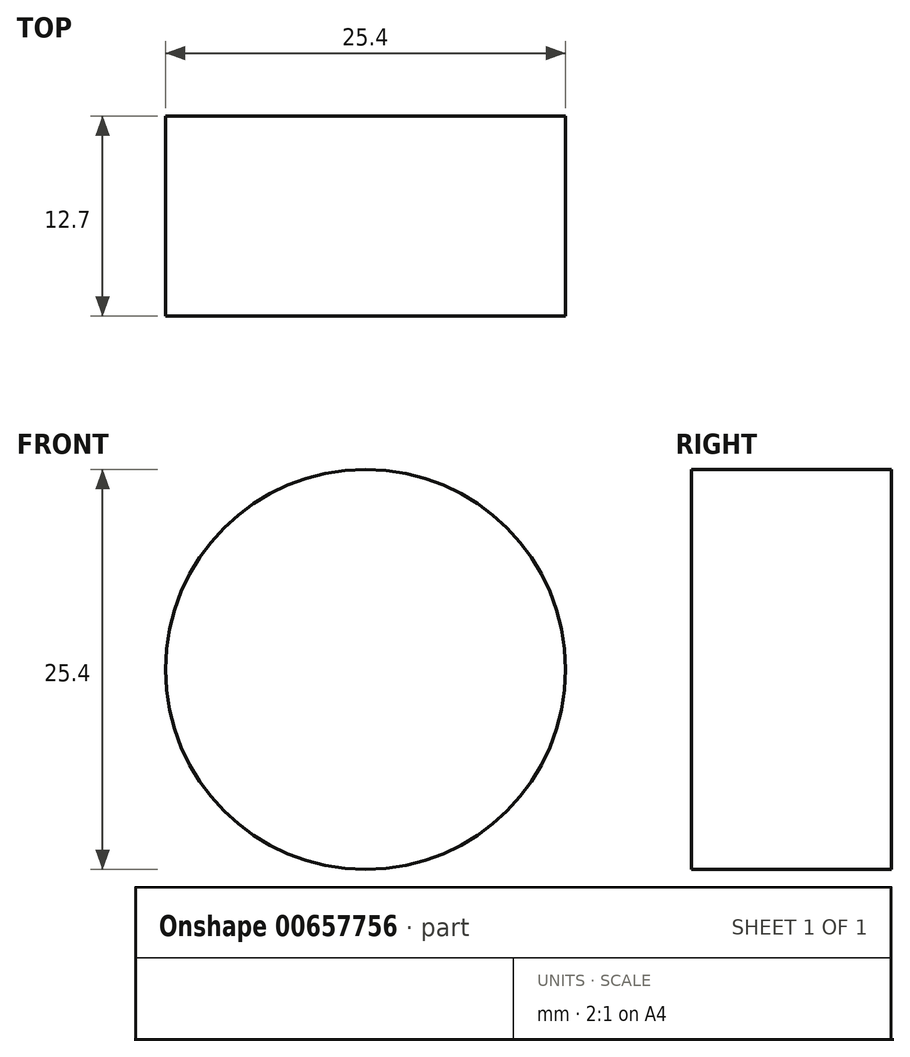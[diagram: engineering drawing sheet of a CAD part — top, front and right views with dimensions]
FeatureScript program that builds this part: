
annotation { "Feature Type Name" : "Feature", "Feature Type Description" : "" }
export const myFeature = defineFeature(function(context is Context, id is Id, definition is map)
    precondition{}
    {
        {
            var Q0;
            Q0=qCreatedBy(makeId("Front.planeOp"),FACE);
            var sketch = newSketch(context, id + "F0", { "sketchPlane" : qUnion([Q0])});
            skCircle(sketch, "E0", {"center": v(0, 0) * mm, "radius": 12.7 * mm});
            skCircle(sketch, "E1", {"center": v(0, 0) * mm, "radius": 19.05 * mm});
            skPoint(sketch, "E1.first.point", {"position": v(-11.38, 15.28) * mm});
            skPoint(sketch, "E1.second.point", {"position": v(12.29, -14.56) * mm});
            skPoint(sketch, "E1.third.point", {"position": v(10.08, 16.16) * mm});
            skSolve(sketch);
        }
        {
            var Q0;
            Q0=makeQuery(id+"F0.imprint","IMPRINT",FACE,{"disambiguationData":[TD([[makeQuery(id+"F0.imprint","IMPRINT",EDGE,{"derivedFrom":sQuery(id+"F0.wireOp",EDGE,"E0")}),1.0]])]});
            extrude(context, id + "F1", {"entities" : qUnion([Q0]), "endBound" : BoundingType.SYMMETRIC, "depth" : 12.7 * mm, "offsetDistance" : 25.4 * mm});
        }
    });
